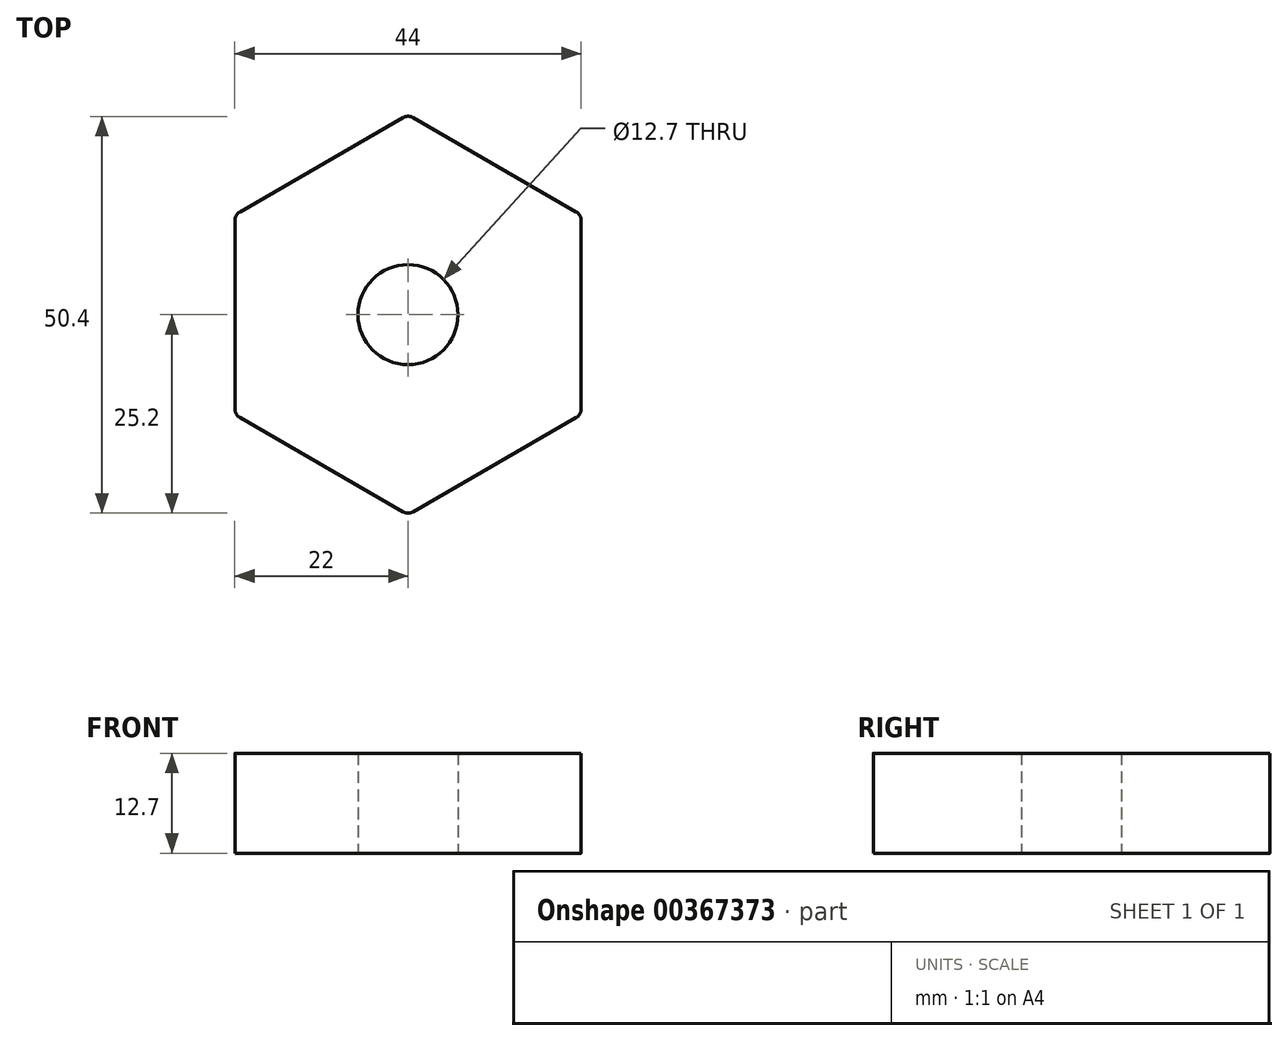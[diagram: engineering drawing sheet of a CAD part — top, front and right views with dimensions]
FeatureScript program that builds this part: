
annotation { "Feature Type Name" : "Feature", "Feature Type Description" : "" }
export const myFeature = defineFeature(function(context is Context, id is Id, definition is map)
    precondition{}
    {
        {
            var Q0;
            Q0=qCreatedBy(makeId("Top.planeOp"),FACE);
            var sketch = newSketch(context, id + "F0", { "sketchPlane" : qUnion([Q0])});
            skLineSegment(sketch, "E0", {"start": v(-22, -12.7) * mm, "end": v(0, -25.4) * mm});
            skLineSegment(sketch, "E1", {"start": v(0, -25.4) * mm, "end": v(22, -12.7) * mm});
            skLineSegment(sketch, "E2", {"start": v(22, -12.7) * mm, "end": v(22, 12.7) * mm});
            skLineSegment(sketch, "E3", {"start": v(22, 12.7) * mm, "end": v(0, 25.4) * mm});
            skLineSegment(sketch, "E4", {"start": v(0, 25.4) * mm, "end": v(-22, 12.7) * mm});
            skLineSegment(sketch, "E5", {"start": v(-22, 12.7) * mm, "end": v(-22, -12.7) * mm});
            skCircle(sketch, "E6", {"center": v(0, 0) * mm, "radius": 22 * mm, "construction": true});
            skCircle(sketch, "E7", {"center": v(0, 0) * mm, "radius": 6.35 * mm});
            skSolve(sketch);
        }
        {
            var Q0;
            Q0=makeQuery(id+"F0.imprint","IMPRINT",FACE,{"disambiguationData":[TD([[makeQuery(id+"F0.imprint","IMPRINT",EDGE,{"derivedFrom":sQuery(id+"F0.wireOp",EDGE,"E0")}),1.0]])]});
            extrude(context, id + "F1", {"entities" : qUnion([Q0]), "depth" : 12.7 * mm});
        }
        {
            var Q0;
            Q0=makeQuery(id+"F1.opExtrude","SWEPT_EDGE",EDGE,{"disambiguationData":[OSD([sQuery(id+"F0.wireOp",EDGE,"E1"),sQuery(id+"F0.wireOp",EDGE,"E2")])]});
            var Q1;
            Q1=makeQuery(id+"F1.opExtrude","SWEPT_EDGE",EDGE,{"disambiguationData":[OSD([sQuery(id+"F0.wireOp",EDGE,"E0"),sQuery(id+"F0.wireOp",EDGE,"E1")])]});
            var Q2;
            Q2=makeQuery(id+"F1.opExtrude","SWEPT_EDGE",EDGE,{"disambiguationData":[OSD([sQuery(id+"F0.wireOp",EDGE,"E2"),sQuery(id+"F0.wireOp",EDGE,"E3")])]});
            var Q3;
            Q3=makeQuery(id+"F1.opExtrude","SWEPT_EDGE",EDGE,{"disambiguationData":[OSD([sQuery(id+"F0.wireOp",EDGE,"E0"),sQuery(id+"F0.wireOp",EDGE,"E5")])]});
            var Q4;
            Q4=makeQuery(id+"F1.opExtrude","SWEPT_EDGE",EDGE,{"disambiguationData":[OSD([sQuery(id+"F0.wireOp",EDGE,"E4"),sQuery(id+"F0.wireOp",EDGE,"E5")])]});
            var Q5;
            Q5=makeQuery(id+"F1.opExtrude","SWEPT_EDGE",EDGE,{"disambiguationData":[OSD([sQuery(id+"F0.wireOp",EDGE,"E3"),sQuery(id+"F0.wireOp",EDGE,"E4")])]});
            fillet(context, id + "F2", {"entities" : qUnion([Q0, Q1, Q2, Q3, Q4, Q5]), "radius" : 1.27 * mm, "tangentPropagation" : true, "allowEdgeOverflow" : false});
        }
    });
